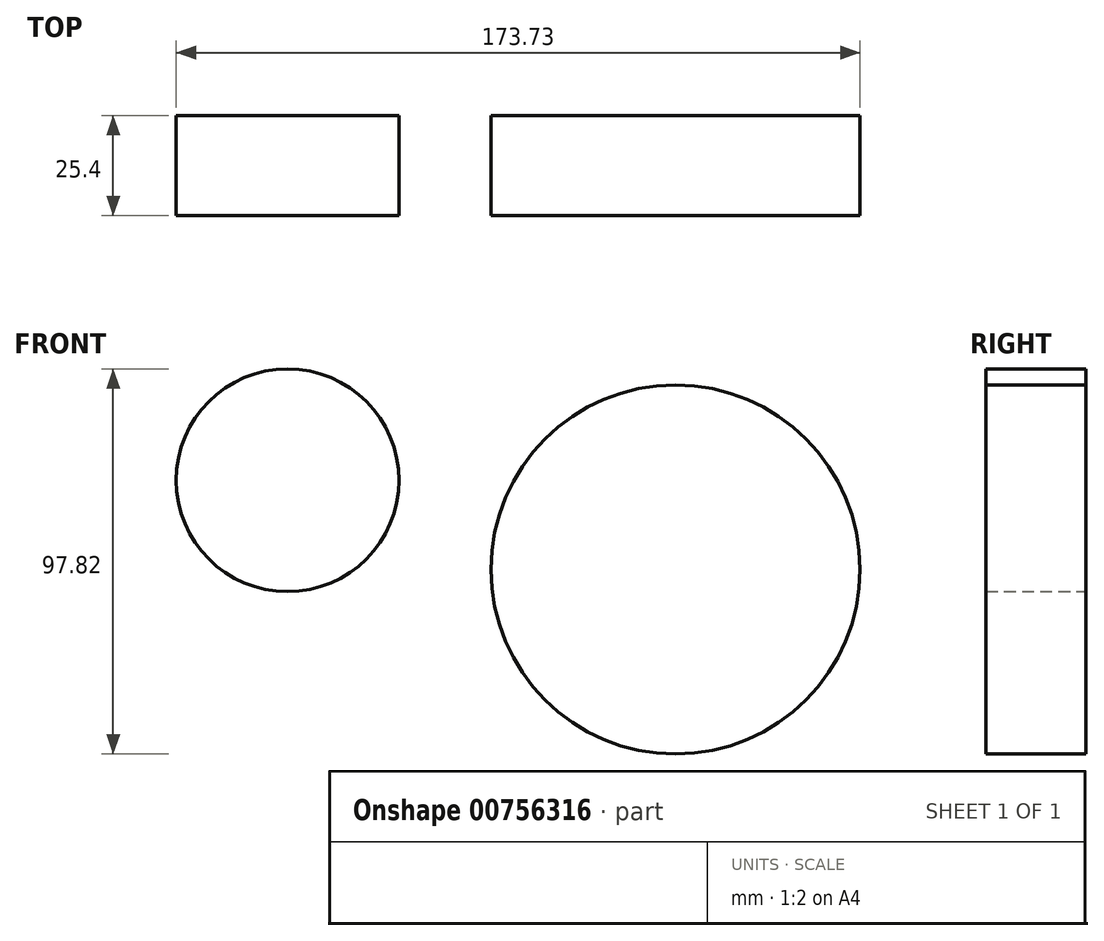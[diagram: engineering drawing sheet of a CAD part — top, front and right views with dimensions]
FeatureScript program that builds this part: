
annotation { "Feature Type Name" : "Feature", "Feature Type Description" : "" }
export const myFeature = defineFeature(function(context is Context, id is Id, definition is map)
    precondition{}
    {
        {
            var Q0;
            Q0=qCreatedBy(makeId("Front.planeOp"),FACE);
            var sketch = newSketch(context, id + "F0", { "sketchPlane" : qUnion([Q0])});
            skCircle(sketch, "E0", {"center": v(0, 0) * mm, "radius": 46.88 * mm});
            skSolve(sketch);
        }
        {
            var Q0;
            Q0=qCreatedBy(makeId("Front.planeOp"),FACE);
            var sketch = newSketch(context, id + "F1", { "sketchPlane" : qUnion([Q0])});
            skCircle(sketch, "E1", {"center": v(0, 0) * mm, "radius": 24.27 * mm});
            skCircle(sketch, "E2", {"center": v(0, 0) * mm, "radius": 7.84 * mm});
            skSolve(sketch);
        }
        {
            var Q0;
            Q0=makeQuery(id+"F1.imprint","IMPRINT",FACE,{"disambiguationData":[TD([[makeQuery(id+"F1.imprint","IMPRINT",EDGE,{"derivedFrom":sQuery(id+"F1.wireOp",EDGE,"E1")}),1.0]])]});
            extrude(context, id + "F2", {"entities" : qUnion([Q0]), "depth" : 25.4 * mm, "offsetDistance" : 25.4 * mm});
        }
        {
            var Q0;
            Q0=makeQuery(id+"F2.opExtrude","CAP_EDGE",EDGE,{"disambiguationData":[OSD([sQuery(id+"F1.wireOp",EDGE,"E1")])],"isStart":true});
            var Q1;
            Q1=makeQuery(id+"F2.opExtrude","CAP_EDGE",EDGE,{"disambiguationData":[OSD([sQuery(id+"F1.wireOp",EDGE,"E1")])],"isStart":false});
            loft(context, id + "F3", {"bodyType" : ToolBodyType.SURFACE, "wireProfilesArray" : [{ "wireProfileEntities" : qUnion([Q0]) }, { "wireProfileEntities" : qUnion([Q1]) }]});
        }
        {
            var Q0;
            Q0=makeQuery(id+"F0.imprint","IMPRINT",FACE,{"disambiguationData":[TD([[makeQuery(id+"F0.imprint","IMPRINT",EDGE,{"derivedFrom":sQuery(id+"F0.wireOp",EDGE,"E0")}),1.0]])]});
            extrude(context, id + "F4", {"entities" : qUnion([Q0]), "operationType" : NewBodyOperationType.ADD, "depth" : 25.4 * mm, "offsetDistance" : 25.4 * mm});
        }
        {
            var Q0;
            Q0=qCreatedBy(makeId("Front.planeOp"),FACE);
            var sketch = newSketch(context, id + "F5", { "sketchPlane" : qUnion([Q0])});
            skCircle(sketch, "E3", {"center": v(-98.56, 22.65) * mm, "radius": 28.29 * mm});
            skCircle(sketch, "E4", {"center": v(-98.56, 22.65) * mm, "radius": 20.41 * mm});
            skCircle(sketch, "E5", {"center": v(-98.56, 22.65) * mm, "radius": 10.02 * mm});
            skSolve(sketch);
        }
        {
            var Q0;
            Q0=makeQuery(id+"F5.imprint","IMPRINT",FACE,{"disambiguationData":[TD([[makeQuery(id+"F5.imprint","IMPRINT",EDGE,{"derivedFrom":sQuery(id+"F5.wireOp",EDGE,"E3")}),1.0]])]});
            var Q1;
            Q1=makeQuery(id+"F5.imprint","IMPRINT",FACE,{"disambiguationData":[TD([[makeQuery(id+"F5.imprint","IMPRINT",EDGE,{"derivedFrom":sQuery(id+"F5.wireOp",EDGE,"E5")}),1.0]])]});
            var Q2;
            Q2 = qSketchRegion(id + "F5", true);
            var Q3;
            Q3=makeQuery(id+"F5.imprint","IMPRINT",FACE,{"disambiguationData":[TD([[makeQuery(id+"F5.imprint","IMPRINT",EDGE,{"derivedFrom":sQuery(id+"F5.wireOp",EDGE,"E4")}),1.0]])]});
            extrude(context, id + "F6", {"entities" : qUnion([Q0, Q1, Q2, Q3]), "depth" : 25.4 * mm, "offsetDistance" : 25.4 * mm});
        }
        {
            var Q0;
            Q0=qCreatedBy(makeId("Front.planeOp"),FACE);
            var sketch = newSketch(context, id + "F7", { "sketchPlane" : qUnion([Q0])});
            skFitSpline(sketch, "E6", {"points": [v(0, -47.38) * mm, v(-101.86, -7.32) * mm, v(-125.04, 10.38) * mm, v(-127.28, 34.22) * mm, v(-106.83, 50.74) * mm, v(0, 48.3) * mm, v(37.87, 29.24) * mm, v(48.87, 0) * mm, v(36.62, -30.73) * mm, v(0, -47.38) * mm]});
            skSolve(sketch);
        }
        {
            var Q0;
            Q0=sQuery(id+"F7.wireOp",EDGE,"E6");
            extrude(context, id + "F8", {"bodyType" : ToolBodyType.SURFACE, "surfaceEntities" : qUnion([Q0]), "depth" : 25.4 * mm, "offsetDistance" : 25.4 * mm});
        }
        {
            var Q0;
            Q0=qCreatedBy(makeId("Front.planeOp"),FACE);
            var sketch = newSketch(context, id + "F9", { "sketchPlane" : qUnion([Q0])});
            skCircle(sketch, "E7", {"center": v(-99.47, 18.36) * mm, "radius": 16.97 * mm});
            skSolve(sketch);
        }
        {
            var Q0;
            Q0=sQuery(id+"F9.wireOp",EDGE,"E7");
            extrude(context, id + "F10", {"bodyType" : ToolBodyType.SURFACE, "surfaceEntities" : qUnion([Q0]), "depth" : 25.4 * mm, "offsetDistance" : 25.4 * mm});
        }
    });
